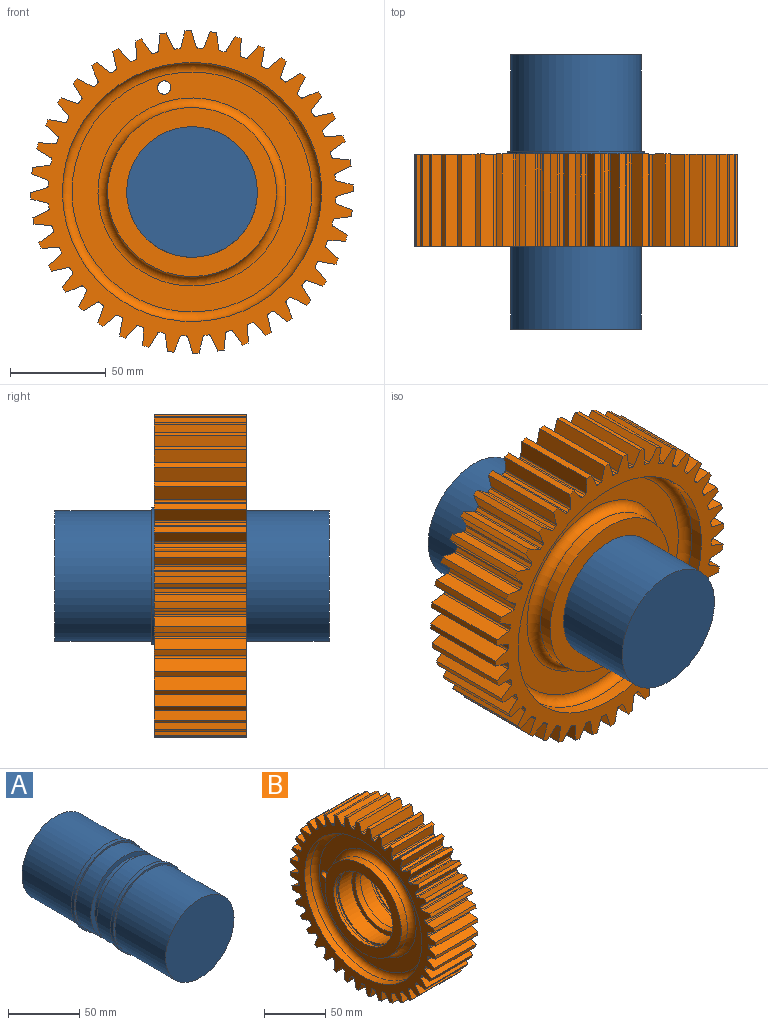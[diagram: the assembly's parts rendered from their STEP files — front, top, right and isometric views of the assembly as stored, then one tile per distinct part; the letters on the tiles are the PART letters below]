
ASSEMBLY  parts=2 mates=1
PART A: 15 faces, bbox 71x142.9x71 mm
  f0: plane 71x71mm, normal (0,-1,0), area 327.5mm2, adj f1,f7
  f1: cylinder r=34mm len=68mm, axis (0,-1,0), area 10775.1mm2, adj f0,f2
  f2: plane 68x68mm, normal (0,-1,0), area 3631.7mm2, adj f1
  f3: cylinder r=30mm len=60mm, axis (0,-1,0), area 1131mm2, adj f4,f11
  f4: plane 68x68mm, normal (0,1,0), area 804.2mm2, adj f3,f5
  f5: cylinder r=34mm len=68mm, axis (0,-1,0), area 3204.4mm2, adj f4,f6
  f6: plane 71x71mm, normal (0,1,0), area 327.5mm2, adj f5,f7
  f7: cylinder r=35.5mm len=71mm, axis (0,-1,0), area 669.2mm2, adj f0,f6
  f8: plane 71x71mm, normal (0,1,0), area 327.5mm2, adj f9,f14
  f9: cylinder r=34mm len=68mm, axis (0,1,0), area 10775.1mm2, adj f8,f10
  f10: plane 68x68mm, normal (0,1,0), area 3631.7mm2, adj f9
  f11: plane 68x68mm, normal (0,-1,0), area 804.2mm2, adj f3,f12
  f12: cylinder r=34mm len=68mm, axis (0,1,0), area 3204.4mm2, adj f11,f13
  f13: plane 71x71mm, normal (0,-1,0), area 327.5mm2, adj f12,f14
  f14: cylinder r=35.5mm len=71mm, axis (0,1,0), area 669.2mm2, adj f8,f13
PART B: 268 faces, bbox 48x167.7x167.7 mm
  f0: cylinder r=84mm len=48mm, axis (-1,0,0), area 155.9mm2, adj f5,f7,f260,f261
  f1: plane 48x8.57mm, normal (0,0.98,0.19), area 419mm2, adj f2,f234,f260,f261
  f2: cylinder r=1mm len=48mm, axis (1,0,0), area 59.3mm2, adj f1,f3,f260,f261
  f3: cylinder r=75mm len=48mm, axis (1,0,0), area 99mm2, adj f2,f4,f260,f261
  f4: cylinder r=1mm len=48mm, axis (1,0,0), area 59.3mm2, adj f3,f5,f260,f261
  f5: plane 48x7.63mm, normal (0,-0.87,0.48), area 419mm2, adj f0,f4,f260,f261
  f6: cylinder r=84mm len=48mm, axis (-1,0,0), area 155.9mm2, adj f11,f13,f260,f261
  f7: plane 48x8.72mm, normal (0,1,0.03), area 419mm2, adj f0,f8,f260,f261
  f8: cylinder r=1mm len=48mm, axis (1,0,0), area 59.3mm2, adj f7,f9,f260,f261
  f9: cylinder r=75mm len=48mm, axis (1,0,0), area 99mm2, adj f8,f10,f260,f261
  f10: cylinder r=1mm len=48mm, axis (1,0,0), area 59.3mm2, adj f9,f11,f260,f261
  f11: plane 48x6.88mm, normal (0,-0.79,0.62), area 419mm2, adj f6,f10,f260,f261
  f12: cylinder r=84mm len=48mm, axis (-1,0,0), area 155.9mm2, adj f17,f19,f260,f261
  f13: plane 48x8.66mm, normal (0,0.99,-0.12), area 419mm2, adj f6,f14,f260,f261
  f14: cylinder r=1mm len=48mm, axis (1,0,0), area 59.3mm2, adj f13,f15,f260,f261
  f15: cylinder r=75mm len=48mm, axis (1,0,0), area 99mm2, adj f14,f16,f260,f261
  f16: cylinder r=1mm len=48mm, axis (1,0,0), area 59.3mm2, adj f15,f17,f260,f261
  f17: plane 48x6.38mm, normal (0,-0.68,0.73), area 419mm2, adj f12,f16,f260,f261
  f18: cylinder r=84mm len=48mm, axis (-1,0,0), area 155.9mm2, adj f23,f25,f260,f261
  f19: plane 48x8.39mm, normal (0,0.96,-0.28), area 419mm2, adj f12,f20,f260,f261
  f20: cylinder r=1mm len=48mm, axis (1,0,0), area 59.3mm2, adj f19,f21,f260,f261
  f21: cylinder r=75mm len=48mm, axis (1,0,0), area 99mm2, adj f20,f22,f260,f261
  f22: cylinder r=1mm len=48mm, axis (1,0,0), area 59.3mm2, adj f21,f23,f260,f261
  f23: plane 48x7.24mm, normal (0,-0.56,0.83), area 419mm2, adj f18,f22,f260,f261
  f24: cylinder r=84mm len=48mm, axis (-1,0,0), area 155.9mm2, adj f29,f31,f260,f261
  f25: plane 48x7.91mm, normal (0,0.91,-0.42), area 419mm2, adj f18,f26,f260,f261
  f26: cylinder r=1mm len=48mm, axis (1,0,0), area 59.3mm2, adj f25,f27,f260,f261
  f27: cylinder r=75mm len=48mm, axis (1,0,0), area 99mm2, adj f26,f28,f260,f261
  f28: cylinder r=1mm len=48mm, axis (1,0,0), area 59.3mm2, adj f27,f29,f260,f261
  f29: plane 48x7.91mm, normal (0,-0.42,0.91), area 419mm2, adj f24,f28,f260,f261
  f30: cylinder r=84mm len=48mm, axis (-1,0,0), area 155.9mm2, adj f35,f37,f260,f261
  f31: plane 48x7.24mm, normal (0,0.83,-0.56), area 419mm2, adj f24,f32,f260,f261
  f32: cylinder r=1mm len=48mm, axis (1,0,0), area 59.3mm2, adj f31,f33,f260,f261
  f33: cylinder r=75mm len=48mm, axis (1,0,0), area 99mm2, adj f32,f34,f260,f261
  f34: cylinder r=1mm len=48mm, axis (1,0,0), area 59.3mm2, adj f33,f35,f260,f261
  f35: plane 48x8.39mm, normal (0,-0.28,0.96), area 419mm2, adj f30,f34,f260,f261
  f36: cylinder r=84mm len=48mm, axis (-1,0,0), area 155.9mm2, adj f41,f43,f260,f261
  f37: plane 48x6.38mm, normal (0,0.73,-0.68), area 419mm2, adj f30,f38,f260,f261
  f38: cylinder r=1mm len=48mm, axis (1,0,0), area 59.3mm2, adj f37,f39,f260,f261
  f39: cylinder r=75mm len=48mm, axis (1,0,0), area 99mm2, adj f38,f40,f260,f261
  f40: cylinder r=1mm len=48mm, axis (1,0,0), area 59.3mm2, adj f39,f41,f260,f261
  f41: plane 48x8.66mm, normal (0,-0.12,0.99), area 419mm2, adj f36,f40,f260,f261
  f42: cylinder r=84mm len=48mm, axis (-1,0,0), area 155.9mm2, adj f47,f49,f260,f261
  f43: plane 48x6.88mm, normal (0,0.62,-0.79), area 419mm2, adj f36,f44,f260,f261
  f44: cylinder r=1mm len=48mm, axis (1,0,0), area 59.3mm2, adj f43,f45,f260,f261
  f45: cylinder r=75mm len=48mm, axis (1,0,0), area 99mm2, adj f44,f46,f260,f261
  f46: cylinder r=1mm len=48mm, axis (1,0,0), area 59.3mm2, adj f45,f47,f260,f261
  f47: plane 48x8.72mm, normal (0,0.03,1), area 419mm2, adj f42,f46,f260,f261
  f48: cylinder r=84mm len=48mm, axis (-1,0,0), area 155.9mm2, adj f53,f55,f260,f261
  f49: plane 48x7.63mm, normal (0,0.48,-0.87), area 419mm2, adj f42,f50,f260,f261
  f50: cylinder r=1mm len=48mm, axis (1,0,0), area 59.3mm2, adj f49,f51,f260,f261
  f51: cylinder r=75mm len=48mm, axis (1,0,0), area 99mm2, adj f50,f52,f260,f261
  f52: cylinder r=1mm len=48mm, axis (1,0,0), area 59.3mm2, adj f51,f53,f260,f261
  f53: plane 48x8.57mm, normal (0,0.19,0.98), area 419mm2, adj f48,f52,f260,f261
  f54: cylinder r=84mm len=48mm, axis (-1,0,0), area 155.9mm2, adj f59,f61,f260,f261
  f55: plane 48x8.2mm, normal (0,0.34,-0.94), area 419mm2, adj f48,f56,f260,f261
  f56: cylinder r=1mm len=48mm, axis (1,0,0), area 59.3mm2, adj f55,f57,f260,f261
  f57: cylinder r=75mm len=48mm, axis (1,0,0), area 99mm2, adj f56,f58,f260,f261
  f58: cylinder r=1mm len=48mm, axis (1,0,0), area 59.3mm2, adj f57,f59,f260,f261
  f59: plane 48x8.2mm, normal (0,0.34,0.94), area 419mm2, adj f54,f58,f260,f261
  f60: cylinder r=84mm len=48mm, axis (-1,0,0), area 155.9mm2, adj f65,f67,f260,f261
  f61: plane 48x8.57mm, normal (0,0.19,-0.98), area 419mm2, adj f54,f62,f260,f261
  f62: cylinder r=1mm len=48mm, axis (1,0,0), area 59.3mm2, adj f61,f63,f260,f261
  f63: cylinder r=75mm len=48mm, axis (1,0,0), area 99mm2, adj f62,f64,f260,f261
  f64: cylinder r=1mm len=48mm, axis (1,0,0), area 59.3mm2, adj f63,f65,f260,f261
  f65: plane 48x7.63mm, normal (0,0.48,0.87), area 419mm2, adj f60,f64,f260,f261
  f66: cylinder r=84mm len=48mm, axis (-1,0,0), area 155.9mm2, adj f71,f73,f260,f261
  f67: plane 48x8.72mm, normal (0,0.03,-1), area 419mm2, adj f60,f68,f260,f261
  f68: cylinder r=1mm len=48mm, axis (1,0,0), area 59.3mm2, adj f67,f69,f260,f261
  f69: cylinder r=75mm len=48mm, axis (1,0,0), area 99mm2, adj f68,f70,f260,f261
  f70: cylinder r=1mm len=48mm, axis (1,0,0), area 59.3mm2, adj f69,f71,f260,f261
  f71: plane 48x6.88mm, normal (0,0.62,0.79), area 419mm2, adj f66,f70,f260,f261
  f72: cylinder r=84mm len=48mm, axis (-1,0,0), area 155.9mm2, adj f77,f79,f260,f261
  f73: plane 48x8.66mm, normal (0,-0.12,-0.99), area 419mm2, adj f66,f74,f260,f261
  f74: cylinder r=1mm len=48mm, axis (1,0,0), area 59.3mm2, adj f73,f75,f260,f261
  f75: cylinder r=75mm len=48mm, axis (1,0,0), area 99mm2, adj f74,f76,f260,f261
  f76: cylinder r=1mm len=48mm, axis (1,0,0), area 59.3mm2, adj f75,f77,f260,f261
  f77: plane 48x6.38mm, normal (0,0.73,0.68), area 419mm2, adj f72,f76,f260,f261
  f78: cylinder r=84mm len=48mm, axis (-1,0,0), area 155.9mm2, adj f83,f85,f260,f261
  f79: plane 48x8.39mm, normal (0,-0.28,-0.96), area 419mm2, adj f72,f80,f260,f261
  f80: cylinder r=1mm len=48mm, axis (1,0,0), area 59.3mm2, adj f79,f81,f260,f261
  f81: cylinder r=75mm len=48mm, axis (1,0,0), area 99mm2, adj f80,f82,f260,f261
  f82: cylinder r=1mm len=48mm, axis (1,0,0), area 59.3mm2, adj f81,f83,f260,f261
  f83: plane 48x7.24mm, normal (0,0.83,0.56), area 419mm2, adj f78,f82,f260,f261
  f84: cylinder r=84mm len=48mm, axis (-1,0,0), area 155.9mm2, adj f89,f91,f260,f261
  f85: plane 48x7.91mm, normal (0,-0.42,-0.91), area 419mm2, adj f78,f86,f260,f261
  f86: cylinder r=1mm len=48mm, axis (1,0,0), area 59.3mm2, adj f85,f87,f260,f261
  f87: cylinder r=75mm len=48mm, axis (1,0,0), area 99mm2, adj f86,f88,f260,f261
  f88: cylinder r=1mm len=48mm, axis (1,0,0), area 59.3mm2, adj f87,f89,f260,f261
  f89: plane 48x7.91mm, normal (0,0.91,0.42), area 419mm2, adj f84,f88,f260,f261
  f90: cylinder r=84mm len=48mm, axis (-1,0,0), area 155.9mm2, adj f95,f97,f260,f261
  f91: plane 48x7.24mm, normal (0,-0.56,-0.83), area 419mm2, adj f84,f92,f260,f261
  f92: cylinder r=1mm len=48mm, axis (1,0,0), area 59.3mm2, adj f91,f93,f260,f261
  f93: cylinder r=75mm len=48mm, axis (1,0,0), area 99mm2, adj f92,f94,f260,f261
  f94: cylinder r=1mm len=48mm, axis (1,0,0), area 59.3mm2, adj f93,f95,f260,f261
  f95: plane 48x8.39mm, normal (0,0.96,0.28), area 419mm2, adj f90,f94,f260,f261
  f96: cylinder r=84mm len=48mm, axis (-1,0,0), area 155.9mm2, adj f101,f103,f260,f261
  f97: plane 48x6.38mm, normal (0,-0.68,-0.73), area 419mm2, adj f90,f98,f260,f261
  f98: cylinder r=1mm len=48mm, axis (1,0,0), area 59.3mm2, adj f97,f99,f260,f261
  f99: cylinder r=75mm len=48mm, axis (1,0,0), area 99mm2, adj f98,f100,f260,f261
  f100: cylinder r=1mm len=48mm, axis (1,0,0), area 59.3mm2, adj f99,f101,f260,f261
  f101: plane 48x8.66mm, normal (0,0.99,0.12), area 419mm2, adj f96,f100,f260,f261
  f102: cylinder r=84mm len=48mm, axis (-1,0,0), area 155.9mm2, adj f107,f109,f260,f261
  f103: plane 48x6.88mm, normal (0,-0.79,-0.62), area 419mm2, adj f96,f104,f260,f261
  f104: cylinder r=1mm len=48mm, axis (1,0,0), area 59.3mm2, adj f103,f105,f260,f261
  f105: cylinder r=75mm len=48mm, axis (1,0,0), area 99mm2, adj f104,f106,f260,f261
  f106: cylinder r=1mm len=48mm, axis (1,0,0), area 59.3mm2, adj f105,f107,f260,f261
  f107: plane 48x8.72mm, normal (0,1,-0.03), area 419mm2, adj f102,f106,f260,f261
  f108: cylinder r=84mm len=48mm, axis (-1,0,0), area 155.9mm2, adj f113,f115,f260,f261
  f109: plane 48x7.63mm, normal (0,-0.87,-0.48), area 419mm2, adj f102,f110,f260,f261
  f110: cylinder r=1mm len=48mm, axis (1,0,0), area 59.3mm2, adj f109,f111,f260,f261
  f111: cylinder r=75mm len=48mm, axis (1,0,0), area 99mm2, adj f110,f112,f260,f261
  f112: cylinder r=1mm len=48mm, axis (1,0,0), area 59.3mm2, adj f111,f113,f260,f261
  f113: plane 48x8.57mm, normal (0,0.98,-0.19), area 419mm2, adj f108,f112,f260,f261
  f114: cylinder r=84mm len=48mm, axis (-1,0,0), area 155.9mm2, adj f119,f121,f260,f261
  f115: plane 48x8.2mm, normal (0,-0.94,-0.34), area 419mm2, adj f108,f116,f260,f261
  f116: cylinder r=1mm len=48mm, axis (1,0,0), area 59.3mm2, adj f115,f117,f260,f261
  f117: cylinder r=75mm len=48mm, axis (1,0,0), area 99mm2, adj f116,f118,f260,f261
  f118: cylinder r=1mm len=48mm, axis (1,0,0), area 59.3mm2, adj f117,f119,f260,f261
  f119: plane 48x8.2mm, normal (0,0.94,-0.34), area 419mm2, adj f114,f118,f260,f261
  f120: cylinder r=84mm len=48mm, axis (-1,0,0), area 155.9mm2, adj f125,f127,f260,f261
  f121: plane 48x8.57mm, normal (0,-0.98,-0.19), area 419mm2, adj f114,f122,f260,f261
  f122: cylinder r=1mm len=48mm, axis (1,0,0), area 59.3mm2, adj f121,f123,f260,f261
  f123: cylinder r=75mm len=48mm, axis (1,0,0), area 99mm2, adj f122,f124,f260,f261
  f124: cylinder r=1mm len=48mm, axis (1,0,0), area 59.3mm2, adj f123,f125,f260,f261
  f125: plane 48x7.63mm, normal (0,0.87,-0.48), area 419mm2, adj f120,f124,f260,f261
  f126: cylinder r=84mm len=48mm, axis (-1,0,0), area 155.9mm2, adj f131,f133,f260,f261
  f127: plane 48x8.72mm, normal (0,-1,-0.03), area 419mm2, adj f120,f128,f260,f261
  f128: cylinder r=1mm len=48mm, axis (1,0,0), area 59.3mm2, adj f127,f129,f260,f261
  f129: cylinder r=75mm len=48mm, axis (1,0,0), area 99mm2, adj f128,f130,f260,f261
  f130: cylinder r=1mm len=48mm, axis (1,0,0), area 59.3mm2, adj f129,f131,f260,f261
  f131: plane 48x6.88mm, normal (0,0.79,-0.62), area 419mm2, adj f126,f130,f260,f261
  f132: cylinder r=84mm len=48mm, axis (-1,0,0), area 155.9mm2, adj f137,f139,f260,f261
  f133: plane 48x8.66mm, normal (0,-0.99,0.12), area 419mm2, adj f126,f134,f260,f261
  f134: cylinder r=1mm len=48mm, axis (1,0,0), area 59.3mm2, adj f133,f135,f260,f261
  f135: cylinder r=75mm len=48mm, axis (1,0,0), area 99mm2, adj f134,f136,f260,f261
  f136: cylinder r=1mm len=48mm, axis (1,0,0), area 59.3mm2, adj f135,f137,f260,f261
  f137: plane 48x6.38mm, normal (0,0.68,-0.73), area 419mm2, adj f132,f136,f260,f261
  f138: cylinder r=84mm len=48mm, axis (-1,0,0), area 155.9mm2, adj f143,f145,f260,f261
  f139: plane 48x8.39mm, normal (0,-0.96,0.28), area 419mm2, adj f132,f140,f260,f261
  f140: cylinder r=1mm len=48mm, axis (1,0,0), area 59.3mm2, adj f139,f141,f260,f261
  f141: cylinder r=75mm len=48mm, axis (1,0,0), area 99mm2, adj f140,f142,f260,f261
  f142: cylinder r=1mm len=48mm, axis (1,0,0), area 59.3mm2, adj f141,f143,f260,f261
  f143: plane 48x7.24mm, normal (0,0.56,-0.83), area 419mm2, adj f138,f142,f260,f261
  f144: cylinder r=84mm len=48mm, axis (-1,0,0), area 155.9mm2, adj f149,f151,f260,f261
  f145: plane 48x7.91mm, normal (0,-0.91,0.42), area 419mm2, adj f138,f146,f260,f261
  f146: cylinder r=1mm len=48mm, axis (1,0,0), area 59.3mm2, adj f145,f147,f260,f261
  f147: cylinder r=75mm len=48mm, axis (1,0,0), area 99mm2, adj f146,f148,f260,f261
  f148: cylinder r=1mm len=48mm, axis (1,0,0), area 59.3mm2, adj f147,f149,f260,f261
  f149: plane 48x7.91mm, normal (0,0.42,-0.91), area 419mm2, adj f144,f148,f260,f261
  f150: cylinder r=84mm len=48mm, axis (-1,0,0), area 155.9mm2, adj f155,f157,f260,f261
  f151: plane 48x7.24mm, normal (0,-0.83,0.56), area 419mm2, adj f144,f152,f260,f261
  f152: cylinder r=1mm len=48mm, axis (1,0,0), area 59.3mm2, adj f151,f153,f260,f261
  f153: cylinder r=75mm len=48mm, axis (1,0,0), area 99mm2, adj f152,f154,f260,f261
  f154: cylinder r=1mm len=48mm, axis (1,0,0), area 59.3mm2, adj f153,f155,f260,f261
  f155: plane 48x8.39mm, normal (0,0.28,-0.96), area 419mm2, adj f150,f154,f260,f261
  f156: cylinder r=84mm len=48mm, axis (-1,0,0), area 155.9mm2, adj f161,f163,f260,f261
  f157: plane 48x6.38mm, normal (0,-0.73,0.68), area 419mm2, adj f150,f158,f260,f261
  f158: cylinder r=1mm len=48mm, axis (1,0,0), area 59.3mm2, adj f157,f159,f260,f261
  f159: cylinder r=75mm len=48mm, axis (1,0,0), area 99mm2, adj f158,f160,f260,f261
  f160: cylinder r=1mm len=48mm, axis (1,0,0), area 59.3mm2, adj f159,f161,f260,f261
  f161: plane 48x8.66mm, normal (0,0.12,-0.99), area 419mm2, adj f156,f160,f260,f261
  f162: cylinder r=84mm len=48mm, axis (-1,0,0), area 155.9mm2, adj f167,f169,f260,f261
  f163: plane 48x6.88mm, normal (0,-0.62,0.79), area 419mm2, adj f156,f164,f260,f261
  f164: cylinder r=1mm len=48mm, axis (1,0,0), area 59.3mm2, adj f163,f165,f260,f261
  f165: cylinder r=75mm len=48mm, axis (1,0,0), area 99mm2, adj f164,f166,f260,f261
  f166: cylinder r=1mm len=48mm, axis (1,0,0), area 59.3mm2, adj f165,f167,f260,f261
  f167: plane 48x8.72mm, normal (0,-0.03,-1), area 419mm2, adj f162,f166,f260,f261
  f168: cylinder r=84mm len=48mm, axis (-1,0,0), area 155.9mm2, adj f173,f175,f260,f261
  f169: plane 48x7.63mm, normal (0,-0.48,0.87), area 419mm2, adj f162,f170,f260,f261
  f170: cylinder r=1mm len=48mm, axis (1,0,0), area 59.3mm2, adj f169,f171,f260,f261
  f171: cylinder r=75mm len=48mm, axis (1,0,0), area 99mm2, adj f170,f172,f260,f261
  f172: cylinder r=1mm len=48mm, axis (1,0,0), area 59.3mm2, adj f171,f173,f260,f261
  f173: plane 48x8.57mm, normal (0,-0.19,-0.98), area 419mm2, adj f168,f172,f260,f261
  f174: cylinder r=84mm len=48mm, axis (-1,0,0), area 155.9mm2, adj f179,f181,f260,f261
  f175: plane 48x8.2mm, normal (0,-0.34,0.94), area 419mm2, adj f168,f176,f260,f261
  f176: cylinder r=1mm len=48mm, axis (1,0,0), area 59.3mm2, adj f175,f177,f260,f261
  f177: cylinder r=75mm len=48mm, axis (1,0,0), area 99mm2, adj f176,f178,f260,f261
  f178: cylinder r=1mm len=48mm, axis (1,0,0), area 59.3mm2, adj f177,f179,f260,f261
  f179: plane 48x8.2mm, normal (0,-0.34,-0.94), area 419mm2, adj f174,f178,f260,f261
  f180: cylinder r=84mm len=48mm, axis (-1,0,0), area 155.9mm2, adj f185,f187,f260,f261
  f181: plane 48x8.57mm, normal (0,-0.19,0.98), area 419mm2, adj f174,f182,f260,f261
  f182: cylinder r=1mm len=48mm, axis (1,0,0), area 59.3mm2, adj f181,f183,f260,f261
  f183: cylinder r=75mm len=48mm, axis (1,0,0), area 99mm2, adj f182,f184,f260,f261
  f184: cylinder r=1mm len=48mm, axis (1,0,0), area 59.3mm2, adj f183,f185,f260,f261
  f185: plane 48x7.63mm, normal (0,-0.48,-0.87), area 419mm2, adj f180,f184,f260,f261
  f186: cylinder r=84mm len=48mm, axis (-1,0,0), area 155.9mm2, adj f191,f193,f260,f261
  f187: plane 48x8.72mm, normal (0,-0.03,1), area 419mm2, adj f180,f188,f260,f261
  f188: cylinder r=1mm len=48mm, axis (1,0,0), area 59.3mm2, adj f187,f189,f260,f261
  f189: cylinder r=75mm len=48mm, axis (1,0,0), area 99mm2, adj f188,f190,f260,f261
  f190: cylinder r=1mm len=48mm, axis (1,0,0), area 59.3mm2, adj f189,f191,f260,f261
  f191: plane 48x6.88mm, normal (0,-0.62,-0.79), area 419mm2, adj f186,f190,f260,f261
  f192: cylinder r=84mm len=48mm, axis (-1,0,0), area 155.9mm2, adj f197,f199,f260,f261
  f193: plane 48x8.66mm, normal (0,0.12,0.99), area 419mm2, adj f186,f194,f260,f261
  f194: cylinder r=1mm len=48mm, axis (1,0,0), area 59.3mm2, adj f193,f195,f260,f261
  f195: cylinder r=75mm len=48mm, axis (1,0,0), area 99mm2, adj f194,f196,f260,f261
  f196: cylinder r=1mm len=48mm, axis (1,0,0), area 59.3mm2, adj f195,f197,f260,f261
  f197: plane 48x6.38mm, normal (0,-0.73,-0.68), area 419mm2, adj f192,f196,f260,f261
  f198: cylinder r=84mm len=48mm, axis (-1,0,0), area 155.9mm2, adj f203,f205,f260,f261
  f199: plane 48x8.39mm, normal (0,0.28,0.96), area 419mm2, adj f192,f200,f260,f261
  f200: cylinder r=1mm len=48mm, axis (1,0,0), area 59.3mm2, adj f199,f201,f260,f261
  f201: cylinder r=75mm len=48mm, axis (1,0,0), area 99mm2, adj f200,f202,f260,f261
  f202: cylinder r=1mm len=48mm, axis (1,0,0), area 59.3mm2, adj f201,f203,f260,f261
  f203: plane 48x7.24mm, normal (0,-0.83,-0.56), area 419mm2, adj f198,f202,f260,f261
  f204: cylinder r=84mm len=48mm, axis (-1,0,0), area 155.9mm2, adj f209,f211,f260,f261
  f205: plane 48x7.91mm, normal (0,0.42,0.91), area 419mm2, adj f198,f206,f260,f261
  f206: cylinder r=1mm len=48mm, axis (1,0,0), area 59.3mm2, adj f205,f207,f260,f261
  f207: cylinder r=75mm len=48mm, axis (1,0,0), area 99mm2, adj f206,f208,f260,f261
  f208: cylinder r=1mm len=48mm, axis (1,0,0), area 59.3mm2, adj f207,f209,f260,f261
  f209: plane 48x7.91mm, normal (0,-0.91,-0.42), area 419mm2, adj f204,f208,f260,f261
  f210: cylinder r=84mm len=48mm, axis (-1,0,0), area 155.9mm2, adj f215,f217,f260,f261
  f211: plane 48x7.24mm, normal (0,0.56,0.83), area 419mm2, adj f204,f212,f260,f261
  f212: cylinder r=1mm len=48mm, axis (1,0,0), area 59.3mm2, adj f211,f213,f260,f261
  f213: cylinder r=75mm len=48mm, axis (1,0,0), area 99mm2, adj f212,f214,f260,f261
  f214: cylinder r=1mm len=48mm, axis (1,0,0), area 59.3mm2, adj f213,f215,f260,f261
  f215: plane 48x8.39mm, normal (0,-0.96,-0.28), area 419mm2, adj f210,f214,f260,f261
  f216: cylinder r=84mm len=48mm, axis (-1,0,0), area 155.9mm2, adj f221,f223,f260,f261
  f217: plane 48x6.38mm, normal (0,0.68,0.73), area 419mm2, adj f210,f218,f260,f261
  f218: cylinder r=1mm len=48mm, axis (1,0,0), area 59.3mm2, adj f217,f219,f260,f261
  f219: cylinder r=75mm len=48mm, axis (1,0,0), area 99mm2, adj f218,f220,f260,f261
  f220: cylinder r=1mm len=48mm, axis (1,0,0), area 59.3mm2, adj f219,f221,f260,f261
  f221: plane 48x8.66mm, normal (0,-0.99,-0.12), area 419mm2, adj f216,f220,f260,f261
  f222: cylinder r=84mm len=48mm, axis (-1,0,0), area 155.9mm2, adj f227,f229,f260,f261
  f223: plane 48x6.88mm, normal (0,0.79,0.62), area 419mm2, adj f216,f224,f260,f261
  f224: cylinder r=1mm len=48mm, axis (1,0,0), area 59.3mm2, adj f223,f225,f260,f261
  f225: cylinder r=75mm len=48mm, axis (1,0,0), area 99mm2, adj f224,f226,f260,f261
  f226: cylinder r=1mm len=48mm, axis (1,0,0), area 59.3mm2, adj f225,f227,f260,f261
  f227: plane 48x8.72mm, normal (0,-1,0.03), area 419mm2, adj f222,f226,f260,f261
  f228: cylinder r=84mm len=48mm, axis (-1,0,0), area 155.9mm2, adj f233,f260,f261,f262
  f229: plane 48x7.63mm, normal (0,0.87,0.48), area 419mm2, adj f222,f230,f260,f261
  f230: cylinder r=1mm len=48mm, axis (1,0,0), area 59.3mm2, adj f229,f231,f260,f261
  f231: cylinder r=75mm len=48mm, axis (1,0,0), area 99mm2, adj f230,f232,f260,f261
  f232: cylinder r=1mm len=48mm, axis (1,0,0), area 59.3mm2, adj f231,f233,f260,f261
  f233: plane 48x8.57mm, normal (0,-0.98,0.19), area 419mm2, adj f228,f232,f260,f261
  f234: cylinder r=84mm len=48mm, axis (-1,0,0), area 155.9mm2, adj f1,f260,f261,f266
  f235: cylinder r=67.5mm len=135mm, axis (-1,0,0), area 2968.8mm2, adj f236,f261
  f236: torus R=62.5mm, axis (-1,0,0), area 3241.3mm2, adj f235,f237
  f237: plane 125x125mm, normal (-1,0,0), area 4691.2mm2, adj f236,f238,f267
  f238: torus R=49mm, axis (-1,0,0), area 2261mm2, adj f237,f239
  f239: cylinder r=44mm len=88mm, axis (-1,0,0), area 1935.2mm2, adj f238,f240
  f240: plane 88x88mm, normal (-1,0,0), area 2450.4mm2, adj f239,f241
  f241: cylinder r=34mm len=68mm, axis (-1,0,0), area 640.9mm2, adj f240,f242
  f242: plane 71x71mm, normal (1,0,0), area 327.5mm2, adj f241,f243
  f243: cylinder r=35.5mm len=71mm, axis (-1,0,0), area 669.2mm2, adj f242,f244
  f244: plane 71x71mm, normal (-1,0,0), area 327.5mm2, adj f243,f245
  f245: cylinder r=34mm len=68mm, axis (-1,0,0), area 3204.4mm2, adj f244,f246
  f246: plane 68x68mm, normal (-1,0,0), area 804.2mm2, adj f245,f247
  f247: cylinder r=30mm len=60mm, axis (-1,0,0), area 1131mm2, adj f246,f248
  f248: plane 68x68mm, normal (1,0,0), area 804.2mm2, adj f247,f249
  f249: cylinder r=34mm len=68mm, axis (-1,0,0), area 3204.4mm2, adj f248,f250
  f250: plane 71x71mm, normal (1,0,0), area 327.5mm2, adj f249,f251
  f251: cylinder r=35.5mm len=71mm, axis (-1,0,0), area 669.2mm2, adj f250,f252
  f252: plane 71x71mm, normal (-1,0,0), area 327.5mm2, adj f251,f253
  f253: cylinder r=34mm len=68mm, axis (-1,0,0), area 640.9mm2, adj f252,f254
  f254: plane 88x88mm, normal (1,0,0), area 2450.4mm2, adj f253,f255
  f255: cylinder r=44mm len=88mm, axis (-1,0,0), area 1935.2mm2, adj f254,f256
  f256: torus R=49mm, axis (-1,0,0), area 2261mm2, adj f255,f257
  f257: plane 125x125mm, normal (1,0,0), area 4691.2mm2, adj f256,f258,f267
  f258: torus R=62.5mm, axis (-1,0,0), area 3241.3mm2, adj f257,f259
  f259: cylinder r=67.5mm len=135mm, axis (-1,0,0), area 2968.8mm2, adj f258,f260
  f260: plane 167.71x167.71mm, normal (1,0,0), area 5441.8mm2, adj f0,f1,f2,f3,f4,f5,f6,f7
  f261: plane 167.71x167.71mm, normal (-1,0,0), area 5441.8mm2, adj f0,f1,f2,f3,f4,f5,f6,f7
  f262: plane 48x8.2mm, normal (0,0.94,0.34), area 419mm2, adj f228,f260,f261,f263
  f263: cylinder r=1mm len=48mm, axis (1,0,0), area 59.3mm2, adj f260,f261,f262,f264
  f264: cylinder r=75mm len=48mm, axis (1,0,0), area 99mm2, adj f260,f261,f263,f265
  f265: cylinder r=1mm len=48mm, axis (1,0,0), area 59.3mm2, adj f260,f261,f264,f266
  f266: plane 48x8.2mm, normal (0,-0.94,0.34), area 419mm2, adj f234,f260,f261,f265
  f267: cylinder r=3.47mm len=24mm, axis (1,0,0), area 522.6mm2, adj f237,f257
PLACE A t=(104.56,-181.7,-73.97)mm fixed
PLACE B rot(axis=(0.62,-0.62,-0.48),128.9deg) t=(104.56,-186.02,-73.97)mm
MATE cylindrical A.f1 <-> B.f0  axis (0,-1,0) through (104.56,-181.7,-73.97)mm
